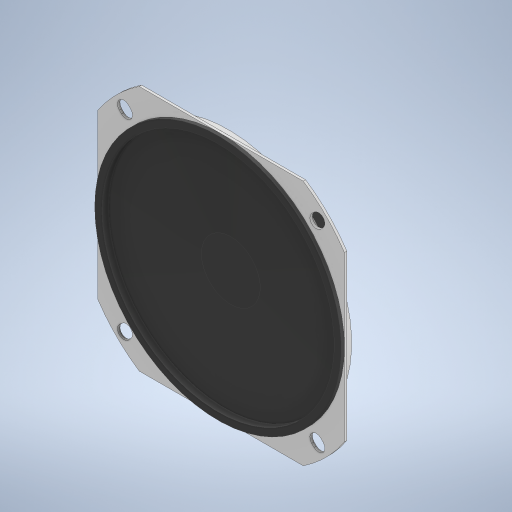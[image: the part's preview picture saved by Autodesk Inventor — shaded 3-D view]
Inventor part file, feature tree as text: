
AUTODESK INVENTOR PART (.ipt)
format: ipt  version: 2023.1 (Build 271208000, 208)  size: 373,248 bytes
history: native  units: mm
features: sketch x4, revolve x3, extrude x2, other x1, pattern_circular x1
ambient origin geometry x8: Origin, YZ Plane, XZ Plane, XY Plane, X Axis, Y Axis, Z Axis, Center Point
bodies: Body1 (feature_tree)
feature tree (11):
  other  "솔리드1"
  extrude  "돌출1"  Depth=92.5mm
  revolve  "회전1"
  sketch  "스케치3"
  revolve  "회전2"
  revolve  "회전3"
  extrude  "돌출2"  Depth=77.0mm
  pattern_circular  "원형 패턴1"  [2 undecoded]
  sketch  "스케치1"
  sketch  "스케치2"
  sketch  "스케치4"
note: 2 required parameter values undecoded (feature->parameter linkage not recoverable at this tier; creation-order binding heuristic only, values carry confidence <= 0.55)
